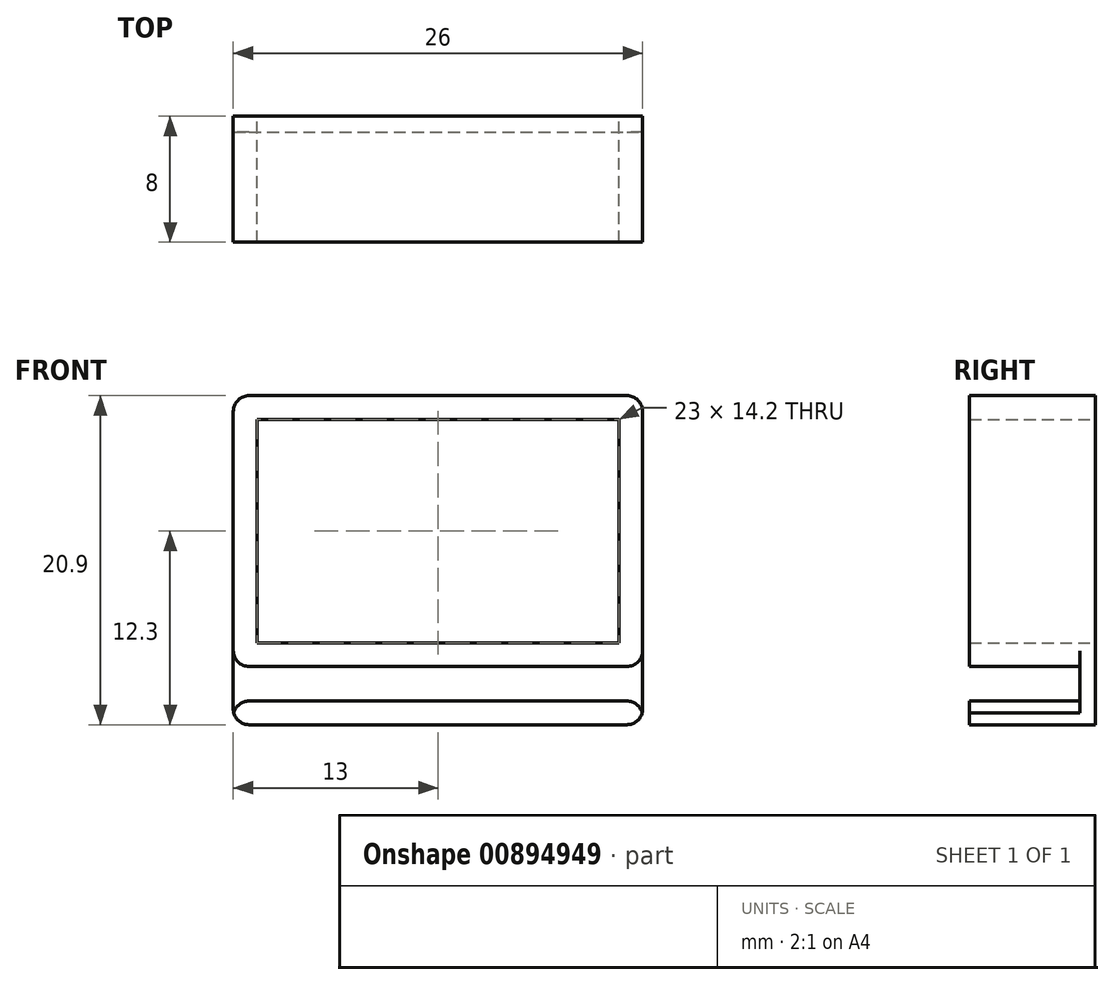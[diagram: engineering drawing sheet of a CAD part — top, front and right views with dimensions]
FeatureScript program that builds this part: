
annotation { "Feature Type Name" : "Feature", "Feature Type Description" : "" }
export const myFeature = defineFeature(function(context is Context, id is Id, definition is map)
    precondition{}
    {
        {
            var Q0;
            Q0=qCreatedBy(makeId("Front.planeOp"),FACE);
            var sketch = newSketch(context, id + "F0", { "sketchPlane" : qUnion([Q0])});
            skLineSegment(sketch, "E0.bottom", {"start": v(11.5, -7.1) * mm, "end": v(-11.5, -7.1) * mm});
            skLineSegment(sketch, "E0.top", {"start": v(11.5, 7.1) * mm, "end": v(-11.5, 7.1) * mm});
            skLineSegment(sketch, "E0.left", {"start": v(11.5, -7.1) * mm, "end": v(11.5, 7.1) * mm});
            skLineSegment(sketch, "E0.right", {"start": v(-11.5, -7.1) * mm, "end": v(-11.5, 7.1) * mm});
            skPoint(sketch, "E0.middle", {"position": v(0, 0) * mm});
            skLineSegment(sketch, "E1.bottom", {"start": v(13, -8.6) * mm, "end": v(-13, -8.6) * mm});
            skLineSegment(sketch, "E1.top", {"start": v(13, 8.6) * mm, "end": v(-13, 8.6) * mm});
            skLineSegment(sketch, "E1.left", {"start": v(13, -8.6) * mm, "end": v(13, 8.6) * mm});
            skLineSegment(sketch, "E1.right", {"start": v(-13, -8.6) * mm, "end": v(-13, 8.6) * mm});
            skLineSegment(sketch, "E2.bottom", {"start": v(-13, -10.8) * mm, "end": v(13, -10.8) * mm});
            skLineSegment(sketch, "E2.top", {"start": v(-13, -12.3) * mm, "end": v(13, -12.3) * mm});
            skLineSegment(sketch, "E2.left", {"start": v(-13, -10.8) * mm, "end": v(-13, -12.3) * mm});
            skLineSegment(sketch, "E2.right", {"start": v(13, -10.8) * mm, "end": v(13, -12.3) * mm});
            skSolve(sketch);
        }
        {
            var Q0;
            Q0 = qSketchRegion(id + "F0", true);
            extrude(context, id + "F1", {"entities" : qUnion([Q0]), "depth" : 8 * mm, "offsetDistance" : 25 * mm});
        }
        {
            var Q0;
            Q0=makeQuery(id+"F1.opExtrude","CAP_FACE",FACE,{"disambiguationData":[OSD([sQuery(id+"F0.wireOp",EDGE,"E2.bottom"),sQuery(id+"F0.wireOp",EDGE,"E2.top"),sQuery(id+"F0.wireOp",EDGE,"E2.left"),sQuery(id+"F0.wireOp",EDGE,"E2.right")])],"isStart":true});
            var sketch = newSketch(context, id + "F2", { "sketchPlane" : qUnion([Q0])});
            skLineSegment(sketch, "E3.bottom", {"start": v(13, -12.3) * mm, "end": v(-13, -12.3) * mm});
            skLineSegment(sketch, "E3.top", {"start": v(13, -7.1) * mm, "end": v(-13, -7.1) * mm});
            skLineSegment(sketch, "E3.left", {"start": v(13, -12.3) * mm, "end": v(13, -7.1) * mm});
            skLineSegment(sketch, "E3.right", {"start": v(-13, -12.3) * mm, "end": v(-13, -7.1) * mm});
            skSolve(sketch);
        }
        {
            var Q0;
            Q0 = qSketchRegion(id + "F2", true);
            extrude(context, id + "F3", {"entities" : qUnion([Q0]), "operationType" : NewBodyOperationType.ADD, "oppositeDirection" : true, "depth" : 1 * mm, "offsetDistance" : 25 * mm});
        }
        {
            var Q0;
            Q0=makeQuery(id+"F1.opExtrude","SWEPT_EDGE",EDGE,{"disambiguationData":[OSD([sQuery(id+"F0.wireOp",EDGE,"E1.bottom"),sQuery(id+"F0.wireOp",EDGE,"E1.right")])]});
            var Q1;
            Q1=makeQuery(id+"F1.opExtrude","SWEPT_EDGE",EDGE,{"disambiguationData":[OSD([sQuery(id+"F0.wireOp",EDGE,"E2.top"),sQuery(id+"F0.wireOp",EDGE,"E2.left")])]});
            var Q2;
            Q2=makeQuery(id+"F1.opExtrude","SWEPT_EDGE",EDGE,{"disambiguationData":[OSD([sQuery(id+"F0.wireOp",EDGE,"E2.top"),sQuery(id+"F0.wireOp",EDGE,"E2.right")])]});
            var Q3;
            Q3=makeQuery(id+"F1.opExtrude","SWEPT_EDGE",EDGE,{"disambiguationData":[OSD([sQuery(id+"F0.wireOp",EDGE,"E1.bottom"),sQuery(id+"F0.wireOp",EDGE,"E1.left")])]});
            var Q4;
            Q4=makeQuery(id+"F1.opExtrude","SWEPT_EDGE",EDGE,{"disambiguationData":[OSD([sQuery(id+"F0.wireOp",EDGE,"E1.top"),sQuery(id+"F0.wireOp",EDGE,"E1.right")])]});
            var Q5;
            Q5=makeQuery(id+"F1.opExtrude","SWEPT_EDGE",EDGE,{"disambiguationData":[OSD([sQuery(id+"F0.wireOp",EDGE,"E1.top"),sQuery(id+"F0.wireOp",EDGE,"E1.left")])]});
            var Q6;
            Q6=makeQuery(id+"F1.opExtrude","SWEPT_EDGE",EDGE,{"disambiguationData":[OSD([sQuery(id+"F0.wireOp",EDGE,"E2.bottom"),sQuery(id+"F0.wireOp",EDGE,"E2.left")])]});
            var Q7;
            Q7=makeQuery(id+"F1.opExtrude","SWEPT_EDGE",EDGE,{"disambiguationData":[OSD([sQuery(id+"F0.wireOp",EDGE,"E2.bottom"),sQuery(id+"F0.wireOp",EDGE,"E2.right")])]});
            fillet(context, id + "F4", {"entities" : qUnion([Q0, Q1, Q2, Q3, Q4, Q5, Q6, Q7]), "radius" : 1 * mm, "tangentPropagation" : true, "allowEdgeOverflow" : false});
        }
    });
